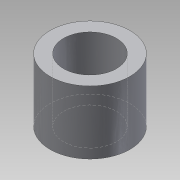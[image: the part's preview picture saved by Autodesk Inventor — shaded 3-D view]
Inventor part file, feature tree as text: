
AUTODESK INVENTOR PART (.ipt)
format: ipt  version: 2013 SP2 (Build 170200200, 200)  size: 79,872 bytes
history: native  units: mm
features: extrude x1, sketch x1
ambient origin geometry x8: Origin, YZ Plane, XZ Plane, XY Plane, X Axis, Y Axis, Z Axis, Center Point
bodies: Solid1 (feature_tree)
feature tree (2):
  extrude  "Extrusion1"  Depth=8.0mm
  sketch  "Sketch1"  dims[d0=5.3mm d1=8.0mm d3=0.0mm]
